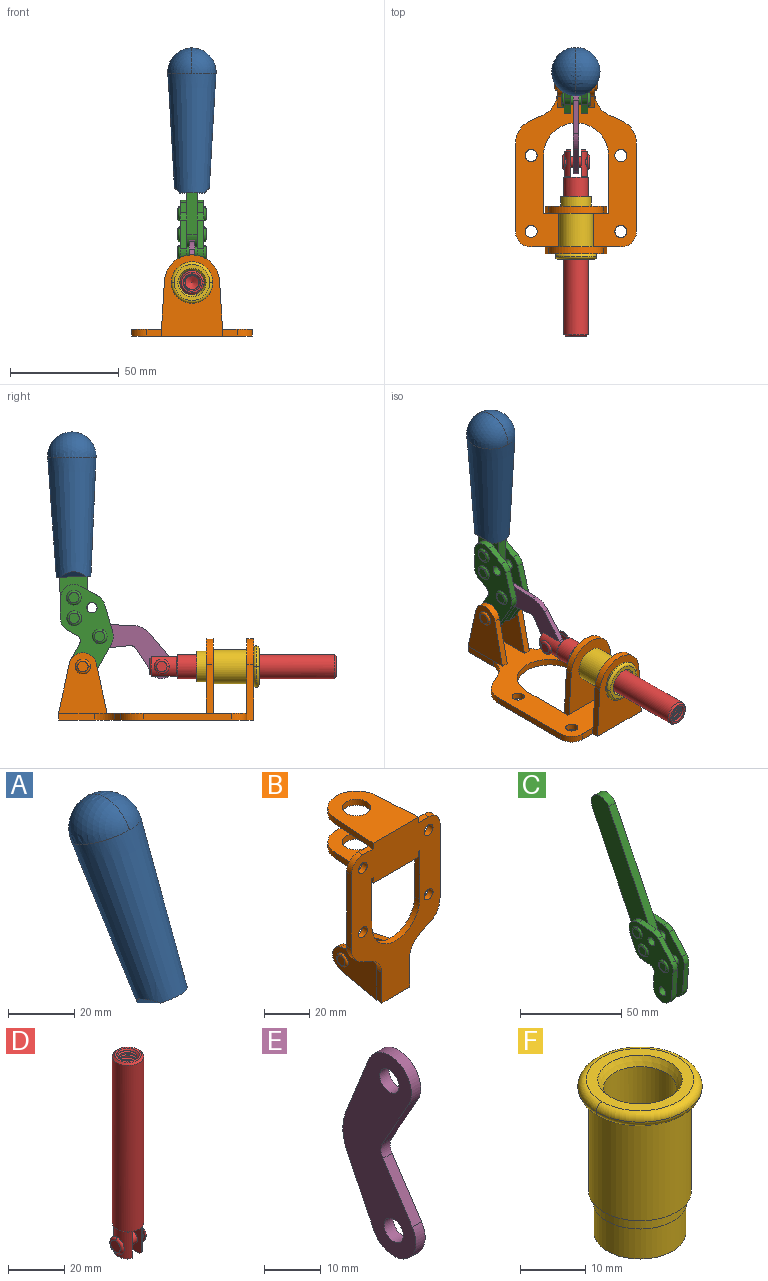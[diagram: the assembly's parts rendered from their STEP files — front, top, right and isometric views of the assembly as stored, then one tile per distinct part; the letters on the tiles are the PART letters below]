
ASSEMBLY  parts=6 mates=6
PART A: 11 faces, bbox 22.3x42.6x64.5 mm
  f0: sphere r=11.13mm, area 411.4mm2, adj f1,f8
  f1: cone r=11.11mm half-angle=3.3deg, axis (0,0.44,0.9), area 3251.8mm2, adj f0,f7,f8,f9,f10
  f2: cylinder r=6.16mm len=11.7mm, axis (1,0,0), area 89.5mm2, adj f3,f4,f5,f6
  f3: plane 60.23x36.75mm, normal (-1,0,0), area 763.6mm2, adj f2,f4,f6,f10
  f4: plane 51.37x25.05mm, normal (0,0.9,-0.44), area 264.2mm2, adj f2,f3,f5,f10
  f5: plane 60.23x36.75mm, normal (1,0,0), area 763.6mm2, adj f2,f4,f6,f10
  f6: plane 51.37x25.05mm, normal (0,-0.9,0.44), area 264.2mm2, adj f2,f3,f5,f10
  f7: plane 9.95x5.95mm, normal (0.71,-0.31,-0.64), area 25.8mm2, adj f1,f10
  f8: sphere r=11.13mm, area 411.4mm2, adj f0,f1
  f9: plane 9.95x5.95mm, normal (-0.71,-0.31,-0.64), area 25.8mm2, adj f1,f10
  f10: plane 14.27x11.38mm, normal (0,-0.44,-0.9), area 106.7mm2, adj f1,f3,f4,f5,f6,f7,f9
PART B: 55 faces, bbox 55.7x37.4x89.8 mm
  f0: torus R=2.41mm, axis (-1,0,0), area 15mm2, adj f11,f15,f25
  f1: torus R=2.41mm, axis (-1,0,0), area 15mm2, adj f10,f12,f22
  f2: cylinder r=2.78mm len=5.56mm, axis (0,-1,0), area 54.2mm2, adj f30,f54
  f3: cylinder r=14.99mm len=29.97mm, axis (0,-1,0), area 145.9mm2, adj f30,f49,f53,f54
  f4: cylinder r=2.78mm len=5.56mm, axis (0,-1,0), area 54.2mm2, adj f30,f54
  f5: cylinder r=2.78mm len=5.56mm, axis (0,-1,0), area 54.2mm2, adj f30,f54
  f6: cylinder r=2.78mm len=5.56mm, axis (0,-1,0), area 54.2mm2, adj f30,f54
  f7: cylinder r=6.35mm len=12.7mm, axis (0,0,1), area 123.6mm2, adj f27,f51
  f8: cylinder r=6.35mm len=12.7mm, axis (0,0,-1), area 124.7mm2, adj f21,f35
  f9: cylinder r=2.41mm len=11.18mm, axis (-1,0,0), area 169.4mm2, adj f16,f19
  f10: plane 4.83x4.83mm, normal (1,0,0), area 18.3mm2, adj f1,f12
  f11: plane 4.83x4.83mm, normal (-1,0,0), area 18.3mm2, adj f0,f15
  f12: torus R=2.41mm, axis (-1,0,0), area 15mm2, adj f1,f10,f22
  f13: cylinder r=6.35mm len=12.41mm, axis (1,0,0), area 53.4mm2, adj f18,f19,f22,f23
  f14: cylinder r=6.35mm len=12.41mm, axis (-1,0,0), area 53.4mm2, adj f16,f17,f24,f25
  f15: torus R=2.41mm, axis (-1,0,0), area 15mm2, adj f0,f11,f25
  f16: plane 27.86x22.35mm, normal (1,0,0), area 425.4mm2, adj f9,f14,f17,f24,f30
  f17: plane 22.86x4.97mm, normal (0,0.21,0.98), area 72.5mm2, adj f14,f16,f25,f30
  f18: plane 22.86x4.97mm, normal (0,0.21,0.98), area 72.5mm2, adj f13,f19,f22,f30
  f19: plane 27.86x22.35mm, normal (-1,0,0), area 425.4mm2, adj f9,f13,f18,f23,f30
  f20: cylinder r=12.7mm len=25.35mm, axis (0,0,-1), area 119.8mm2, adj f21,f34,f35,f36
  f21: plane 34.21x28.07mm, normal (0,0,-1), area 702.4mm2, adj f8,f20,f30,f34,f36
  f22: plane 27.96x22.45mm, normal (1,0,0), area 407.2mm2, adj f1,f12,f13,f18,f23,f30,f42,f43
  f23: plane 22.86x4.97mm, normal (0,0.21,-0.98), area 72.5mm2, adj f13,f19,f22,f44
  f24: plane 22.86x4.97mm, normal (0,0.21,-0.98), area 72.5mm2, adj f14,f16,f25,f44
  f25: plane 27.86x22.35mm, normal (-1,0,0), area 407.1mm2, adj f0,f14,f15,f17,f24,f30,f45,f46
  f26: plane 3.1x0.95mm, normal (0,0,-1), area 2.7mm2, adj f30,f49,f50,f54
  f27: plane 34.21x28.07mm, normal (0,0,1), area 702.4mm2, adj f7,f28,f30,f50,f52
  f28: cylinder r=12.7mm len=25.35mm, axis (0,0,1), area 118.8mm2, adj f27,f50,f51,f52
  f29: plane 3.1x0.95mm, normal (0,0,-1), area 2.7mm2, adj f30,f52,f53,f54
  f30: plane 86.54x55.63mm, normal (0,1,0), area 2362.9mm2, adj f2,f3,f4,f5,f6,f16,f17,f18
  f31: plane 40.56x3.1mm, normal (-1,0,0), area 125.7mm2, adj f30,f32,f48,f54
  f32: cylinder r=7.11mm len=7.11mm, axis (0,-1,0), area 34.6mm2, adj f30,f31,f33,f54
  f33: plane 6.67x3.1mm, normal (0,0,1), area 20.4mm2, adj f30,f32,f34,f54
  f34: plane 25.39x3.13mm, normal (-1,0.06,0), area 79.5mm2, adj f20,f21,f33,f35,f54
  f35: plane 37.31x28.45mm, normal (0,0,1), area 789.9mm2, adj f8,f20,f34,f36,f54
  f36: plane 25.39x3.13mm, normal (1,0.06,0), area 79.5mm2, adj f20,f21,f35,f37,f54
  f37: plane 6.67x3.1mm, normal (0,0,1), area 20.4mm2, adj f30,f36,f38,f54
  f38: cylinder r=7.11mm len=7.11mm, axis (0,-1,0), area 34.6mm2, adj f30,f37,f39,f54
  f39: plane 40.56x3.1mm, normal (1,0,0), area 125.7mm2, adj f30,f38,f40,f54
  f40: cylinder r=11.18mm len=10.16mm, axis (0,-1,0), area 39.5mm2, adj f30,f39,f41,f54
  f41: plane 6.09x3.1mm, normal (0.42,0,-0.91), area 20.8mm2, adj f30,f40,f42,f54
  f42: cylinder r=11.18mm len=9.41mm, axis (0,-1,0), area 37.2mm2, adj f22,f30,f41,f43,f54
  f43: plane 16.5x3.1mm, normal (1,0,0), area 51.1mm2, adj f22,f42,f44,f54
  f44: plane 17.37x3.1mm, normal (0,0,-1), area 53.8mm2, adj f23,f24,f30,f43,f45,f54
  f45: plane 16.5x3.1mm, normal (-1,0,0), area 51.1mm2, adj f25,f44,f46,f54
  f46: cylinder r=11.18mm len=9.41mm, axis (0,-1,0), area 37.2mm2, adj f25,f30,f45,f47,f54
  f47: plane 6.09x3.1mm, normal (-0.42,0,-0.91), area 20.8mm2, adj f30,f46,f48,f54
  f48: cylinder r=11.18mm len=10.16mm, axis (0,-1,0), area 39.5mm2, adj f30,f31,f47,f54
  f49: plane 26.54x3.1mm, normal (-1,0,0), area 82.3mm2, adj f3,f26,f30,f54
  f50: plane 25.39x3.1mm, normal (1,0.06,0), area 78.8mm2, adj f26,f27,f28,f51,f54
  f51: plane 37.31x28.45mm, normal (0,0,-1), area 789.9mm2, adj f7,f28,f50,f52,f54
  f52: plane 25.39x3.1mm, normal (-1,0.06,0), area 78.8mm2, adj f27,f28,f29,f51,f54
  f53: plane 26.54x3.1mm, normal (1,0,0), area 82.3mm2, adj f3,f29,f30,f54
  f54: plane 89.66x55.63mm, normal (0,-1,0), area 2678.5mm2, adj f2,f3,f4,f5,f6,f26,f29,f31
PART C: 59 faces, bbox 12.9x60.2x99.6 mm
  f0: torus R=2.39mm, axis (-1,0,0), area 14.9mm2, adj f20,f43,f51
  f1: torus R=2.39mm, axis (-1,0,0), area 14.9mm2, adj f19,f42,f51
  f2: torus R=2.39mm, axis (-1,0,0), area 14.9mm2, adj f18,f35,f51
  f3: torus R=2.39mm, axis (-1,0,0), area 14.9mm2, adj f14,f17,f23
  f4: torus R=2.39mm, axis (-1,0,0), area 14.9mm2, adj f13,f16,f23
  f5: torus R=2.39mm, axis (-1,0,0), area 14.9mm2, adj f12,f15,f23
  f6: cylinder r=2.39mm len=4.78mm, axis (1,0,0), area 46.5mm2, adj f48,f50,f51
  f7: cylinder r=2.39mm len=4.78mm, axis (1,0,0), area 46.5mm2, adj f50,f51
  f8: cylinder r=6.35mm len=12.68mm, axis (1,0,0), area 61.8mm2, adj f38,f39,f50,f51
  f9: cylinder r=2.39mm len=4.78mm, axis (-1,0,0), area 70.5mm2, adj f46,f50
  f10: cylinder r=2.39mm len=4.78mm, axis (-1,0,0), area 46.5mm2, adj f23,f45,f46
  f11: cylinder r=2.39mm len=4.78mm, axis (-1,0,0), area 46.5mm2, adj f23,f46
  f12: plane 4.78x4.78mm, normal (1,0,0), area 17.9mm2, adj f5,f15
  f13: plane 4.78x4.78mm, normal (1,0,0), area 17.9mm2, adj f4,f16
  f14: plane 4.78x4.78mm, normal (1,0,0), area 17.9mm2, adj f3,f17
  f15: torus R=2.39mm, axis (-1,0,0), area 14.9mm2, adj f5,f12,f23
  f16: torus R=2.39mm, axis (-1,0,0), area 14.9mm2, adj f4,f13,f23
  f17: torus R=2.39mm, axis (-1,0,0), area 14.9mm2, adj f3,f14,f23
  f18: plane 4.78x4.78mm, normal (-1,0,0), area 17.9mm2, adj f2,f35
  f19: plane 4.78x4.78mm, normal (-1,0,0), area 17.9mm2, adj f1,f42
  f20: plane 4.78x4.78mm, normal (-1,0,0), area 17.9mm2, adj f0,f43
  f21: plane 2.26x0.2mm, normal (1,0,0), area 0.2mm2, adj f31,f44
  f22: plane 2.26x0.2mm, normal (-1,0,0), area 0.2mm2, adj f41,f44
  f23: plane 39.37x30.77mm, normal (1,0,0), area 565.5mm2, adj f3,f4,f5,f10,f11,f15,f16,f17
  f24: cylinder r=6.1mm len=4.15mm, axis (-1,0,0), area 14.7mm2, adj f23,f25,f32,f46
  f25: plane 10.25x9.01mm, normal (0,-0.75,0.66), area 42.3mm2, adj f23,f24,f26,f46
  f26: cylinder r=6.35mm len=4.64mm, axis (-1,0,0), area 15.6mm2, adj f23,f25,f27,f46
  f27: plane 15.84x3.1mm, normal (0,-1,-0.07), area 49.2mm2, adj f23,f26,f28,f46
  f28: cylinder r=6.35mm len=12.68mm, axis (-1,0,0), area 61.8mm2, adj f23,f27,f29,f46
  f29: plane 8.11x3.1mm, normal (0,1,0.07), area 25.2mm2, adj f23,f28,f30,f46
  f30: cylinder r=3.05mm len=3.25mm, axis (-1,0,0), area 14.8mm2, adj f23,f29,f31,f46
  f31: plane 5.99x3.1mm, normal (0,0.07,-1), area 18.6mm2, adj f21,f23,f30,f44,f46
  f32: plane 9.5x3.1mm, normal (0,-0.07,1), area 29.5mm2, adj f23,f24,f33,f46,f47
  f33: cylinder r=6.1mm len=8.63mm, axis (-1,0,0), area 39.1mm2, adj f23,f32,f34,f47
  f34: plane 8.65x3.96mm, normal (0,0.91,-0.42), area 29.5mm2, adj f23,f33,f44,f47
  f35: torus R=2.39mm, axis (-1,0,0), area 14.9mm2, adj f2,f18,f51
  f36: plane 10.25x9.01mm, normal (0,-0.75,0.66), area 42.3mm2, adj f37,f49,f50,f51
  f37: cylinder r=6.35mm len=4.64mm, axis (1,0,0), area 15.6mm2, adj f36,f38,f50,f51
  f38: plane 15.84x3.1mm, normal (0,-1,-0.07), area 49.2mm2, adj f8,f37,f50,f51
  f39: plane 8.11x3.1mm, normal (0,1,0.07), area 25.2mm2, adj f8,f40,f50,f51
  f40: cylinder r=3.05mm len=3.25mm, axis (1,0,0), area 14.8mm2, adj f39,f41,f50,f51
  f41: plane 5.99x3.1mm, normal (0,0.07,-1), area 18.6mm2, adj f22,f40,f44,f50,f51
  f42: torus R=2.39mm, axis (-1,0,0), area 14.9mm2, adj f1,f19,f51
  f43: torus R=2.39mm, axis (-1,0,0), area 14.9mm2, adj f0,f20,f51
  f44: cylinder r=6.35mm len=12.12mm, axis (-1,0,0), area 128.9mm2, adj f21,f22,f23,f31,f34,f41,f46,f47
  f45: plane 2.65x1.35mm, normal (1,0,0), area 1mm2, adj f10,f55
  f46: plane 39.08x20.42mm, normal (-1,0,0), area 412.5mm2, adj f9,f10,f11,f24,f25,f26,f27,f28
  f47: plane 77.62x39.82mm, normal (1,0,0), area 850mm2, adj f32,f33,f34,f44,f53,f54,f55
  f48: plane 2.65x1.35mm, normal (-1,0,0), area 1mm2, adj f6,f55
  f49: cylinder r=6.1mm len=4.15mm, axis (1,0,0), area 14.7mm2, adj f36,f50,f51,f56
  f50: plane 39.08x20.42mm, normal (1,0,0), area 412.5mm2, adj f6,f7,f8,f9,f36,f37,f38,f39
  f51: plane 39.37x30.77mm, normal (-1,0,0), area 565.5mm2, adj f0,f1,f2,f6,f7,f8,f35,f36
  f52: plane 8.65x3.96mm, normal (0,0.91,-0.42), area 29.5mm2, adj f44,f51,f57,f58
  f53: plane 68.49x33.4mm, normal (0,0.9,-0.44), area 358.1mm2, adj f44,f47,f54,f58
  f54: cylinder r=6.35mm len=12.06mm, axis (1,0,0), area 93.7mm2, adj f47,f53,f55,f58
  f55: plane 68.49x33.4mm, normal (0,-0.9,0.44), area 358.1mm2, adj f44,f45,f46,f47,f48,f50,f54,f58
  f56: plane 9.5x3.1mm, normal (0,-0.07,1), area 29.5mm2, adj f49,f50,f51,f57,f58
  f57: cylinder r=6.1mm len=8.63mm, axis (1,0,0), area 39.1mm2, adj f51,f52,f56,f58
  f58: plane 77.62x39.82mm, normal (-1,0,0), area 850mm2, adj f44,f52,f53,f54,f55,f56,f57
PART D: 48 faces, bbox 12.6x11.1x86.1 mm
  f0: torus R=2.41mm, axis (-1,0,0), area 15mm2, adj f30,f32,f34
  f1: torus R=2.41mm, axis (-1,0,0), area 15mm2, adj f29,f31,f33
  f2: cylinder r=5.54mm len=72.39mm, axis (0,0,1), area 2518.5mm2, adj f3,f4,f42,f43
  f3: cone r=5.54mm half-angle=45deg, axis (0,0,1), area 7.6mm2, adj f2,f5,f41
  f4: cone r=5.54mm half-angle=45deg, axis (0,0,-1), area 34.9mm2, adj f2,f39
  f5: cylinder r=5.08mm len=11.48mm, axis (0,0,1), area 108.3mm2, adj f3,f7,f8,f41
  f6: cylinder r=2.41mm len=4.83mm, axis (-1,0,0), area 71.2mm2, adj f40,f41
  f7: cylinder r=2.41mm len=4.83mm, axis (-1,0,0), area 7.6mm2, adj f5,f34
  f8: cone r=5.08mm half-angle=45deg, axis (0,0,1), area 10.6mm2, adj f5,f37,f41
  f9: cone r=3.98mm half-angle=45deg, axis (0,0,1), area 17.6mm2, adj f27,f39,f45,f46,f47
  f10: cylinder r=2.41mm len=4.83mm, axis (-1,0,0), area 7.6mm2, adj f33,f38
  f11: cylinder r=3.2mm len=6.4mm, axis (0,0,1), area 78.4mm2, adj f12,f28,f44,f45,f47
  f12: cylinder r=3.2mm len=6.4mm, axis (0,0,1), area 10.5mm2, adj f11,f13,f45,f47
  f13: cylinder r=3.2mm len=6.4mm, axis (0,0,1), area 10.5mm2, adj f12,f14,f45,f47
  f14: cylinder r=3.2mm len=6.4mm, axis (0,0,1), area 10.5mm2, adj f13,f15,f45,f47
  f15: cylinder r=3.2mm len=6.4mm, axis (0,0,1), area 10.5mm2, adj f14,f16,f45,f47
  f16: cylinder r=3.2mm len=6.4mm, axis (0,0,1), area 10.5mm2, adj f15,f17,f45,f47
  f17: cylinder r=3.2mm len=6.4mm, axis (0,0,1), area 10.5mm2, adj f16,f18,f45,f47
  f18: cylinder r=3.2mm len=6.4mm, axis (0,0,1), area 10.5mm2, adj f17,f19,f45,f47
  f19: cylinder r=3.2mm len=6.4mm, axis (0,0,1), area 10.5mm2, adj f18,f20,f45,f47
  f20: cylinder r=3.2mm len=6.4mm, axis (0,0,1), area 10.5mm2, adj f19,f21,f45,f47
  f21: cylinder r=3.2mm len=6.4mm, axis (0,0,1), area 10.5mm2, adj f20,f22,f45,f47
  f22: cylinder r=3.2mm len=6.4mm, axis (0,0,1), area 10.5mm2, adj f21,f23,f45,f47
  f23: cylinder r=3.2mm len=6.4mm, axis (0,0,1), area 10.5mm2, adj f22,f24,f45,f47
  f24: cylinder r=3.2mm len=6.4mm, axis (0,0,1), area 10.5mm2, adj f23,f25,f45,f47
  f25: cylinder r=3.2mm len=6.4mm, axis (0,0,1), area 10.5mm2, adj f24,f26,f45,f47
  f26: cylinder r=3.2mm len=6.4mm, axis (0,0,1), area 10.5mm2, adj f25,f27,f45,f47
  f27: cylinder r=3.2mm len=6.4mm, axis (0,0,1), area 7.4mm2, adj f9,f26,f45,f47
  f28: cone r=3.2mm half-angle=60deg, axis (0,0,1), area 37.2mm2, adj f11
  f29: plane 4.83x4.83mm, normal (-1,0,0), area 18.3mm2, adj f1,f31
  f30: plane 4.83x4.83mm, normal (1,0,0), area 18.3mm2, adj f0,f32
  f31: torus R=2.41mm, axis (-1,0,0), area 15mm2, adj f1,f29,f33
  f32: torus R=2.41mm, axis (-1,0,0), area 15mm2, adj f0,f30,f34
  f33: plane 6.83x6.83mm, normal (1,0,0), area 18.3mm2, adj f1,f10,f31
  f34: plane 6.83x6.83mm, normal (-1,0,0), area 18.3mm2, adj f0,f7,f32
  f35: cone r=5.08mm half-angle=45deg, axis (0,0,1), area 10.6mm2, adj f36,f38,f40
  f36: plane 7.25x1.97mm, normal (0,0,-1), area 10mm2, adj f35,f40
  f37: plane 7.25x1.97mm, normal (0,0,-1), area 10mm2, adj f8,f41
  f38: cylinder r=5.08mm len=11.48mm, axis (0,0,1), area 108.3mm2, adj f10,f35,f40,f42
  f39: plane 9.55x9.55mm, normal (0,0,1), area 22mm2, adj f4,f9
  f40: plane 12.76x10.09mm, normal (1,0,0), area 95.7mm2, adj f6,f35,f36,f38,f42,f43
  f41: plane 12.76x10.09mm, normal (-1,0,0), area 95.7mm2, adj f3,f5,f6,f8,f37,f43
  f42: cone r=5.54mm half-angle=45deg, axis (0,0,1), area 7.6mm2, adj f2,f38,f40
  f43: plane 11.07x4.7mm, normal (0,0,-1), area 50.4mm2, adj f2,f40,f41
  f44: plane 0.89x0.62mm, normal (-1,0,0), area 0.3mm2, adj f11,f45,f46,f47
  f45: bspline ~24.8x7.63mm, area 266.6mm2, adj f9,f11,f12,f13,f14,f15,f16,f17
  f46: bspline ~24.87x7.63mm, area 73.6mm2, adj f9,f44,f45,f47
  f47: bspline ~24.98x7.63mm, area 272.5mm2, adj f9,f11,f12,f13,f14,f15,f16,f17
PART E: 12 faces, bbox 2.3x18.2x42.8 mm
  f0: cylinder r=2.4mm len=4.8mm, axis (1,0,0), area 34.9mm2, adj f4,f11
  f1: cylinder r=10.41mm len=8.47mm, axis (1,0,0), area 20.2mm2, adj f4,f9,f10,f11
  f2: cylinder r=3.05mm len=3.16mm, axis (1,0,0), area 7.7mm2, adj f4,f6,f7,f11
  f3: cylinder r=2.4mm len=4.8mm, axis (1,0,0), area 34.9mm2, adj f4,f11
  f4: plane 42.81x18.23mm, normal (-1,0,0), area 414.1mm2, adj f0,f1,f2,f3,f5,f6,f7,f8
  f5: cylinder r=5.54mm len=10.67mm, axis (1,0,0), area 41.8mm2, adj f4,f6,f10,f11
  f6: plane 11.66x6.53mm, normal (0,-0.87,-0.49), area 30.9mm2, adj f2,f4,f5,f11
  f7: plane 11.17x7.33mm, normal (0,-0.84,0.55), area 30.9mm2, adj f2,f4,f8,f11
  f8: cylinder r=5.54mm len=10.51mm, axis (1,0,0), area 41.8mm2, adj f4,f7,f9,f11
  f9: plane 13.67x6.67mm, normal (0,0.9,-0.44), area 35.1mm2, adj f1,f4,f8,f11
  f10: plane 14.1x5.7mm, normal (0,0.93,0.37), area 35.1mm2, adj f1,f4,f5,f11
  f11: plane 42.81x18.23mm, normal (1,0,0), area 414.1mm2, adj f0,f1,f2,f3,f5,f6,f7,f8
PART F: 15 faces, bbox 20.6x20.6x28.7 mm
  f0: torus R=8.26mm, axis (0,0,1), area 56.8mm2, adj f1,f10,f12
  f1: torus R=8.26mm, axis (0,0,1), area 56.8mm2, adj f0,f6,f13
  f2: cylinder r=5.59mm len=25.91mm, axis (0,0,1), area 909.6mm2, adj f3,f4
  f3: cone r=6.86mm half-angle=45deg, axis (0,0,-1), area 70.2mm2, adj f2,f14
  f4: cone r=6.47mm half-angle=30deg, axis (0,0,1), area 66.7mm2, adj f2,f13
  f5: cylinder r=7.04mm len=14.07mm, axis (0,0,1), area 252.6mm2, adj f11,f14
  f6: torus R=8.26mm, axis (0,0,1), area 56.8mm2, adj f1,f12,f13
  f7: cylinder r=7.16mm len=14.33mm, axis (0,0,1), area 91.5mm2, adj f9,f11
  f8: cylinder r=7.86mm len=18.42mm, axis (0,0,1), area 909.6mm2, adj f9,f10
  f9: plane 15.72x15.72mm, normal (0,0,-1), area 33mm2, adj f7,f8
  f10: plane 16.51x16.51mm, normal (0,0,-1), area 19.9mm2, adj f0,f8,f12
  f11: plane 14.33x14.33mm, normal (0,0,-1), area 5.7mm2, adj f5,f7
  f12: torus R=8.26mm, axis (0,0,1), area 56.8mm2, adj f0,f6,f10
  f13: plane 16.51x16.51mm, normal (0,0,1), area 82.7mm2, adj f1,f4,f6
  f14: plane 14.07x14.07mm, normal (0,0,-1), area 7.8mm2, adj f3,f5
PLACE A rot(axis=(1,0,0),25.2deg) t=(-0.04,5.59,43.18)mm
PLACE B rot(axis=(1,0,0),90deg) t=(0,9.43,0)mm fixed
PLACE C rot(axis=(1,0,0),25.2deg) t=(0,5.59,43.18)mm
PLACE D rot(axis=(1,0,0),90deg) t=(0,20.69,0)mm
PLACE E rot(axis=(0,-0.55,-0.84),180deg) t=(0,29.6,9.7)mm
PLACE F rot(axis=(1,0,0),90deg) t=(0,9.43,0)mm
MATE revolute E.f3 <-> D.f6  axis (-1,0,0) through (0,5.22,24.61)mm
MATE fastened C.f54 <-> A.f2  axis (1,0,0) through (-2.35,46.58,122.98)mm
MATE slider B.f7 <-> D.f2  axis (0,-1,0) through (0,-36.96,24.61)mm
MATE revolute E.f5 <-> C.f4  axis (-1,0,0) through (0,33.78,38.47)mm
MATE revolute C.f7 <-> B.f0  axis (-1,0,0) through (0,41.52,24.61)mm
MATE fastened F.f0 <-> B.f7  axis (0,1,0) through (0,-36.96,24.61)mm
